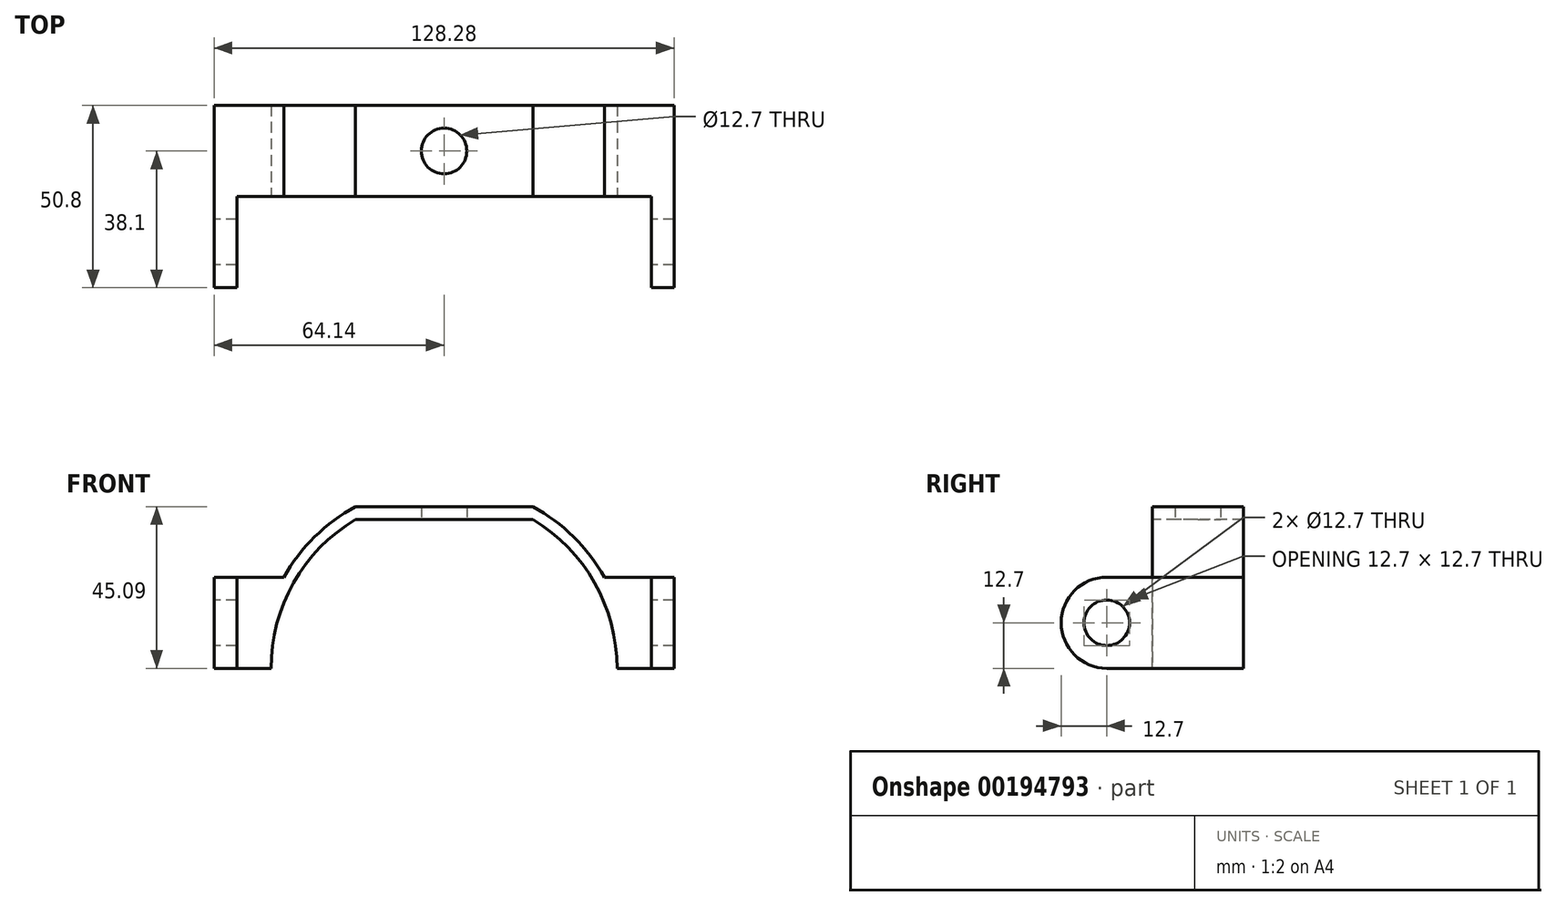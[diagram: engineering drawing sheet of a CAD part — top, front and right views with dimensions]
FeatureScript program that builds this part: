
annotation { "Feature Type Name" : "Feature", "Feature Type Description" : "" }
export const myFeature = defineFeature(function(context is Context, id is Id, definition is map)
    precondition{}
    {
        {
            var Q0;
            Q0=qCreatedBy(makeId("Front.planeOp"),FACE);
            var sketch = newSketch(context, id + "F0", { "sketchPlane" : qUnion([Q0])});
            skCircle(sketch, "E0", {"center": v(0, 0) * mm, "radius": 51.44 * mm});
            skCircle(sketch, "E1", {"center": v(0, 0) * mm, "radius": 48.26 * mm});
            skLineSegment(sketch, "E2", {"start": v(0, 0) * mm, "end": v(51.44, 0) * mm});
            skLineSegment(sketch, "E3", {"start": v(0, 0) * mm, "end": v(-51.44, 0) * mm});
            skLineSegment(sketch, "E4.bottom", {"start": v(44.73, 0) * mm, "end": v(51.44, 0) * mm});
            skLineSegment(sketch, "E4.top", {"start": v(44.73, 25.4) * mm, "end": v(51.44, 25.4) * mm});
            skLineSegment(sketch, "E4.left", {"start": v(44.73, 0) * mm, "end": v(44.73, 25.4) * mm});
            skLineSegment(sketch, "E4.right", {"start": v(51.44, 0) * mm, "end": v(51.44, 25.4) * mm});
            skLineSegment(sketch, "E5.bottom", {"start": v(51.44, 0) * mm, "end": v(57.79, 0) * mm});
            skLineSegment(sketch, "E5.top", {"start": v(51.44, 25.4) * mm, "end": v(57.79, 25.4) * mm});
            skLineSegment(sketch, "E5.right", {"start": v(57.79, 0) * mm, "end": v(57.79, 25.4) * mm});
            skLineSegment(sketch, "E6.bottom", {"start": v(57.79, 0) * mm, "end": v(64.13, 0) * mm});
            skLineSegment(sketch, "E6.top", {"start": v(57.79, 25.4) * mm, "end": v(64.13, 25.4) * mm});
            skLineSegment(sketch, "E6.right", {"start": v(64.13, 0) * mm, "end": v(64.13, 25.4) * mm});
            skLineSegment(sketch, "E7.bottom", {"start": v(-51.44, 0) * mm, "end": v(-44.73, 0) * mm});
            skLineSegment(sketch, "E7.top", {"start": v(-51.44, 25.4) * mm, "end": v(-44.73, 25.4) * mm});
            skLineSegment(sketch, "E7.left", {"start": v(-51.44, 0) * mm, "end": v(-51.44, 25.4) * mm});
            skLineSegment(sketch, "E7.right", {"start": v(-44.73, 0) * mm, "end": v(-44.73, 25.4) * mm});
            skLineSegment(sketch, "E8.bottom", {"start": v(-51.44, 0) * mm, "end": v(-57.78, 0) * mm});
            skLineSegment(sketch, "E8.top", {"start": v(-51.44, 25.4) * mm, "end": v(-57.78, 25.4) * mm});
            skLineSegment(sketch, "E8.right", {"start": v(-57.78, 0) * mm, "end": v(-57.78, 25.4) * mm});
            skLineSegment(sketch, "E9.bottom", {"start": v(-57.78, 0) * mm, "end": v(-64.13, 0) * mm});
            skLineSegment(sketch, "E9.top", {"start": v(-57.78, 25.4) * mm, "end": v(-64.13, 25.4) * mm});
            skLineSegment(sketch, "E9.right", {"start": v(-64.13, 0) * mm, "end": v(-64.13, 25.4) * mm});
            skLineSegment(sketch, "E10.bottom", {"start": v(51.44, 0) * mm, "end": v(-51.44, 0) * mm});
            skLineSegment(sketch, "E10.top", {"start": v(51.44, -57.5) * mm, "end": v(-51.44, -57.5) * mm});
            skLineSegment(sketch, "E10.left", {"start": v(51.44, 0) * mm, "end": v(51.44, -57.5) * mm});
            skLineSegment(sketch, "E10.right", {"start": v(-51.44, 0) * mm, "end": v(-51.44, -57.5) * mm});
            skLineSegment(sketch, "E11", {"start": v(0, 48.26) * mm, "end": v(0, 45.09) * mm});
            skLineSegment(sketch, "E12", {"start": v(0, 45.09) * mm, "end": v(24.76, 45.09) * mm});
            skLineSegment(sketch, "E13", {"start": v(24.76, 45.09) * mm, "end": v(24.76, 41.43) * mm});
            skLineSegment(sketch, "E14", {"start": v(24.76, 41.43) * mm, "end": v(-24.76, 41.43) * mm});
            skLineSegment(sketch, "E15", {"start": v(-24.76, 41.43) * mm, "end": v(-24.76, 45.09) * mm});
            skLineSegment(sketch, "E16", {"start": v(-24.76, 45.09) * mm, "end": v(0, 45.09) * mm});
            skSolve(sketch);
        }
        {
            var Q0;
            {var subQ3=sQuery(id+"F0.wireOp",EDGE,"E7.right");var subQ5=sQuery(id+"F0.wireOp",EDGE,"E1");var subQ6=makeQuery(id+"F0.imprint","INTERSECT",VERTEX,{"derivedFrom":[subQ5,subQ3]});Q0=makeQuery(id+"F0.imprint","IMPRINT",FACE,{"disambiguationData":[TD([[makeQuery(id+"F0.imprint","IMPRINT",EDGE,{"disambiguationData":[TD([[subQ6,-1.0]])],"derivedFrom":subQ5}),-1.0]])]});}
            var Q1;
            {var subQ4=sQuery(id+"F0.wireOp",EDGE,"E7.top");Q1=makeQuery(id+"F0.imprint","IMPRINT",FACE,{"disambiguationData":[TD([[makeQuery(id+"F0.imprint","IMPRINT",EDGE,{"derivedFrom":subQ4}),-1.0]])]});}
            var Q2;
            Q2=makeQuery(id+"F0.imprint","IMPRINT",FACE,{"disambiguationData":[TD([[makeQuery(id+"F0.imprint","IMPRINT",EDGE,{"derivedFrom":sQuery(id+"F0.wireOp",EDGE,"E8.bottom")}),-1.0]])]});
            var Q3;
            Q3=makeQuery(id+"F0.imprint","IMPRINT",FACE,{"disambiguationData":[TD([[makeQuery(id+"F0.imprint","IMPRINT",EDGE,{"derivedFrom":sQuery(id+"F0.wireOp",EDGE,"E9.bottom")}),-1.0]])]});
            var Q4;
            {var subQ0=sQuery(id+"F0.wireOp",EDGE,"E4.left");var subQ1=sQuery(id+"F0.wireOp",EDGE,"E0");var subQ2=makeQuery(id+"F0.imprint","INTERSECT",VERTEX,{"derivedFrom":[subQ1,subQ0]});Q4=makeQuery(id+"F0.imprint","IMPRINT",FACE,{"disambiguationData":[TD([[makeQuery(id+"F0.imprint","IMPRINT",EDGE,{"disambiguationData":[TD([[subQ2,-1.0]])],"derivedFrom":subQ1}),1.0]])]});}
            var Q5;
            {var subQ3=sQuery(id+"F0.wireOp",EDGE,"E4.left");var subQ5=sQuery(id+"F0.wireOp",EDGE,"E1");var subQ6=makeQuery(id+"F0.imprint","INTERSECT",VERTEX,{"derivedFrom":[subQ5,subQ3]});Q5=makeQuery(id+"F0.imprint","IMPRINT",FACE,{"disambiguationData":[TD([[makeQuery(id+"F0.imprint","IMPRINT",EDGE,{"disambiguationData":[TD([[subQ6,1.0]])],"derivedFrom":subQ5}),-1.0]])]});}
            var Q6;
            {var subQ4=sQuery(id+"F0.wireOp",EDGE,"E4.top");Q6=makeQuery(id+"F0.imprint","IMPRINT",FACE,{"disambiguationData":[TD([[makeQuery(id+"F0.imprint","IMPRINT",EDGE,{"derivedFrom":subQ4}),-1.0]])]});}
            var Q7;
            Q7=makeQuery(id+"F0.imprint","IMPRINT",FACE,{"disambiguationData":[TD([[makeQuery(id+"F0.imprint","IMPRINT",EDGE,{"derivedFrom":sQuery(id+"F0.wireOp",EDGE,"E5.bottom")}),1.0]])]});
            var Q8;
            Q8=makeQuery(id+"F0.imprint","IMPRINT",FACE,{"disambiguationData":[TD([[makeQuery(id+"F0.imprint","IMPRINT",EDGE,{"derivedFrom":sQuery(id+"F0.wireOp",EDGE,"E6.bottom")}),1.0]])]});
            var Q9;
            {var subQ0=sQuery(id+"F0.wireOp",EDGE,"E15");Q9=makeQuery(id+"F0.imprint","IMPRINT",FACE,{"disambiguationData":[TD([[makeQuery(id+"F0.imprint","IMPRINT",EDGE,{"derivedFrom":subQ0}),1.0]])]});}
            var Q10;
            {var subQ0=sQuery(id+"F0.wireOp",EDGE,"E14");Q10=makeQuery(id+"F0.imprint","IMPRINT",FACE,{"disambiguationData":[TD([[makeQuery(id+"F0.imprint","IMPRINT",EDGE,{"derivedFrom":subQ0}),-1.0]])]});}
            var Q11;
            {var subQ0=sQuery(id+"F0.wireOp",EDGE,"E15");Q11=makeQuery(id+"F0.imprint","IMPRINT",FACE,{"disambiguationData":[TD([[makeQuery(id+"F0.imprint","IMPRINT",EDGE,{"derivedFrom":subQ0}),-1.0]])]});}
            var Q12;
            {var subQ0=sQuery(id+"F0.wireOp",EDGE,"E13");Q12=makeQuery(id+"F0.imprint","IMPRINT",FACE,{"disambiguationData":[TD([[makeQuery(id+"F0.imprint","IMPRINT",EDGE,{"derivedFrom":subQ0}),-1.0]])]});}
            extrude(context, id + "F1", {"entities" : qUnion([Q0, Q1, Q2, Q3, Q4, Q5, Q6, Q7, Q8, Q9, Q10, Q11, Q12]), "oppositeDirection" : true, "depth" : 25.4 * mm});
        }
        {
            var Q0;
            Q0=makeQuery(id+"F0.imprint","IMPRINT",FACE,{"disambiguationData":[TD([[makeQuery(id+"F0.imprint","IMPRINT",EDGE,{"derivedFrom":sQuery(id+"F0.wireOp",EDGE,"E6.bottom")}),1.0]])]});
            var Q1;
            Q1=makeQuery(id+"F0.imprint","IMPRINT",FACE,{"disambiguationData":[TD([[makeQuery(id+"F0.imprint","IMPRINT",EDGE,{"derivedFrom":sQuery(id+"F0.wireOp",EDGE,"E9.bottom")}),-1.0]])]});
            extrude(context, id + "F2", {"entities" : qUnion([Q0, Q1]), "operationType" : NewBodyOperationType.ADD, "depth" : 25.4 * mm});
        }
        {
            var Q0;
            Q0=qCreatedBy(makeId("Right.planeOp"),FACE);
            var sketch = newSketch(context, id + "F3", { "sketchPlane" : qUnion([Q0])});
            skLineSegment(sketch, "E17", {"start": v(0, 0) * mm, "end": v(0, 25.4) * mm});
            skLineSegment(sketch, "E18.bottom", {"start": v(0, 25.4) * mm, "end": v(-25.4, 25.4) * mm});
            skLineSegment(sketch, "E18.top", {"start": v(0, 0) * mm, "end": v(-25.4, 0) * mm});
            skLineSegment(sketch, "E18.left", {"start": v(0, 25.4) * mm, "end": v(0, 0) * mm});
            skLineSegment(sketch, "E18.right", {"start": v(-25.4, 25.4) * mm, "end": v(-25.4, 0) * mm});
            skLineSegment(sketch, "E19", {"start": v(0, 0) * mm, "end": v(0, 12.7) * mm});
            skLineSegment(sketch, "E20", {"start": v(0, 12.7) * mm, "end": v(-12.7, 12.7) * mm});
            skCircle(sketch, "E21", {"center": v(-12.7, 12.7) * mm, "radius": 12.7 * mm});
            skCircle(sketch, "E22", {"center": v(-12.7, 12.7) * mm, "radius": 6.35 * mm});
            skSolve(sketch);
        }
        {
            var Q0;
            Q0=makeQuery(id+"F3.imprint","IMPRINT",FACE,{"disambiguationData":[TD([[makeQuery(id+"F3.imprint","IMPRINT",EDGE,{"derivedFrom":sQuery(id+"F3.wireOp",EDGE,"E22")}),1.0]])]});
            var Q1;
            {var subQ0=sQuery(id+"F3.wireOp",EDGE,"E18.right");var subQ1=sQuery(id+"F3.wireOp",EDGE,"E18.bottom");var subQ2=makeQuery(id+"F3.imprint","INTERSECT",VERTEX,{"derivedFrom":[subQ1,subQ0]});Q1=makeQuery(id+"F3.imprint","IMPRINT",FACE,{"disambiguationData":[TD([[makeQuery(id+"F3.imprint","IMPRINT",EDGE,{"disambiguationData":[TD([[subQ2,1.0]])],"derivedFrom":subQ1}),1.0]])]});}
            var Q2;
            {var subQ0=sQuery(id+"F3.wireOp",EDGE,"E18.right");var subQ1=sQuery(id+"F3.wireOp",EDGE,"E18.top");var subQ2=makeQuery(id+"F3.imprint","INTERSECT",VERTEX,{"derivedFrom":[subQ1,subQ0]});Q2=makeQuery(id+"F3.imprint","IMPRINT",FACE,{"disambiguationData":[TD([[makeQuery(id+"F3.imprint","IMPRINT",EDGE,{"disambiguationData":[TD([[subQ2,1.0]])],"derivedFrom":subQ1}),-1.0]])]});}
            extrude(context, id + "F4", {"entities" : qUnion([Q0, Q1, Q2]), "endBound" : BoundingType.SYMMETRIC, "depth" : 152.4 * mm});
        }
        {
            var Q0;
            Q0=makeQuery(id+"F4.opExtrude","SWEPT_BODY",BODY,{"disambiguationData":[OSD([sQuery(id+"F3.wireOp",EDGE,"E18.bottom"),sQuery(id+"F3.wireOp",EDGE,"E18.right"),sQuery(id+"F3.wireOp",EDGE,"E21")])]});
            var Q1;
            Q1=makeQuery(id+"F4.opExtrude","SWEPT_BODY",BODY,{"disambiguationData":[OSD([sQuery(id+"F3.wireOp",EDGE,"E22")])]});
            var Q2;
            Q2=makeQuery(id+"F4.opExtrude","SWEPT_BODY",BODY,{"disambiguationData":[OSD([sQuery(id+"F3.wireOp",EDGE,"E18.top"),sQuery(id+"F3.wireOp",EDGE,"E18.right"),sQuery(id+"F3.wireOp",EDGE,"E21")])]});
            var Q3;
            Q3=makeQuery(id+"F1.opExtrude","SWEPT_BODY",BODY,{"disambiguationData":[OSD([sQuery(id+"F0.wireOp",EDGE,"E0"),sQuery(id+"F0.wireOp",EDGE,"E1"),sQuery(id+"F0.wireOp",EDGE,"E4.top"),sQuery(id+"F0.wireOp",EDGE,"E4.left"),sQuery(id+"F0.wireOp",EDGE,"E5.bottom"),sQuery(id+"F0.wireOp",EDGE,"E5.top"),sQuery(id+"F0.wireOp",EDGE,"E6.bottom"),sQuery(id+"F0.wireOp",EDGE,"E6.top"),sQuery(id+"F0.wireOp",EDGE,"E6.right"),sQuery(id+"F0.wireOp",EDGE,"E7.top"),sQuery(id+"F0.wireOp",EDGE,"E7.right"),sQuery(id+"F0.wireOp",EDGE,"E8.bottom"),sQuery(id+"F0.wireOp",EDGE,"E8.top"),sQuery(id+"F0.wireOp",EDGE,"E9.bottom"),sQuery(id+"F0.wireOp",EDGE,"E9.top"),sQuery(id+"F0.wireOp",EDGE,"E9.right"),sQuery(id+"F0.wireOp",EDGE,"E10.bottom")])]});
            booleanBodies(context, id + "F5", {"operationType" : BooleanOperationType.SUBTRACTION, "tools" : qUnion([Q0, Q1, Q2]), "targets" : qUnion([Q3])});
        }
        {
            var Q0;
            Q0=qCreatedBy(makeId("Top.planeOp"),FACE);
            var sketch = newSketch(context, id + "F6", { "sketchPlane" : qUnion([Q0])});
            skLineSegment(sketch, "E23", {"start": v(0, 0) * mm, "end": v(0, 12.7) * mm});
            skCircle(sketch, "E24", {"center": v(0, 12.7) * mm, "radius": 6.35 * mm});
            skSolve(sketch);
        }
        {
            var Q0;
            Q0=makeQuery(id+"F6.imprint","IMPRINT",FACE,{"disambiguationData":[TD([[makeQuery(id+"F6.imprint","IMPRINT",EDGE,{"derivedFrom":sQuery(id+"F6.wireOp",EDGE,"E24")}),1.0]])]});
            extrude(context, id + "F7", {"entities" : qUnion([Q0]), "depth" : 76.2 * mm});
        }
        {
            var Q0;
            Q0=makeQuery(id+"F7.opExtrude","SWEPT_BODY",BODY,{"disambiguationData":[OSD([sQuery(id+"F6.wireOp",EDGE,"E24")])]});
            var Q1;
            Q1=makeQuery(id+"F1.opExtrude","SWEPT_BODY",BODY,{"disambiguationData":[OSD([sQuery(id+"F0.wireOp",EDGE,"E0"),sQuery(id+"F0.wireOp",EDGE,"E1"),sQuery(id+"F0.wireOp",EDGE,"E4.top"),sQuery(id+"F0.wireOp",EDGE,"E4.left"),sQuery(id+"F0.wireOp",EDGE,"E5.bottom"),sQuery(id+"F0.wireOp",EDGE,"E5.top"),sQuery(id+"F0.wireOp",EDGE,"E6.bottom"),sQuery(id+"F0.wireOp",EDGE,"E6.top"),sQuery(id+"F0.wireOp",EDGE,"E6.right"),sQuery(id+"F0.wireOp",EDGE,"E7.top"),sQuery(id+"F0.wireOp",EDGE,"E7.right"),sQuery(id+"F0.wireOp",EDGE,"E8.bottom"),sQuery(id+"F0.wireOp",EDGE,"E8.top"),sQuery(id+"F0.wireOp",EDGE,"E9.bottom"),sQuery(id+"F0.wireOp",EDGE,"E9.top"),sQuery(id+"F0.wireOp",EDGE,"E9.right"),sQuery(id+"F0.wireOp",EDGE,"E10.bottom")])]});
            booleanBodies(context, id + "F8", {"operationType" : BooleanOperationType.SUBTRACTION, "tools" : qUnion([Q0]), "targets" : qUnion([Q1])});
        }
    });
